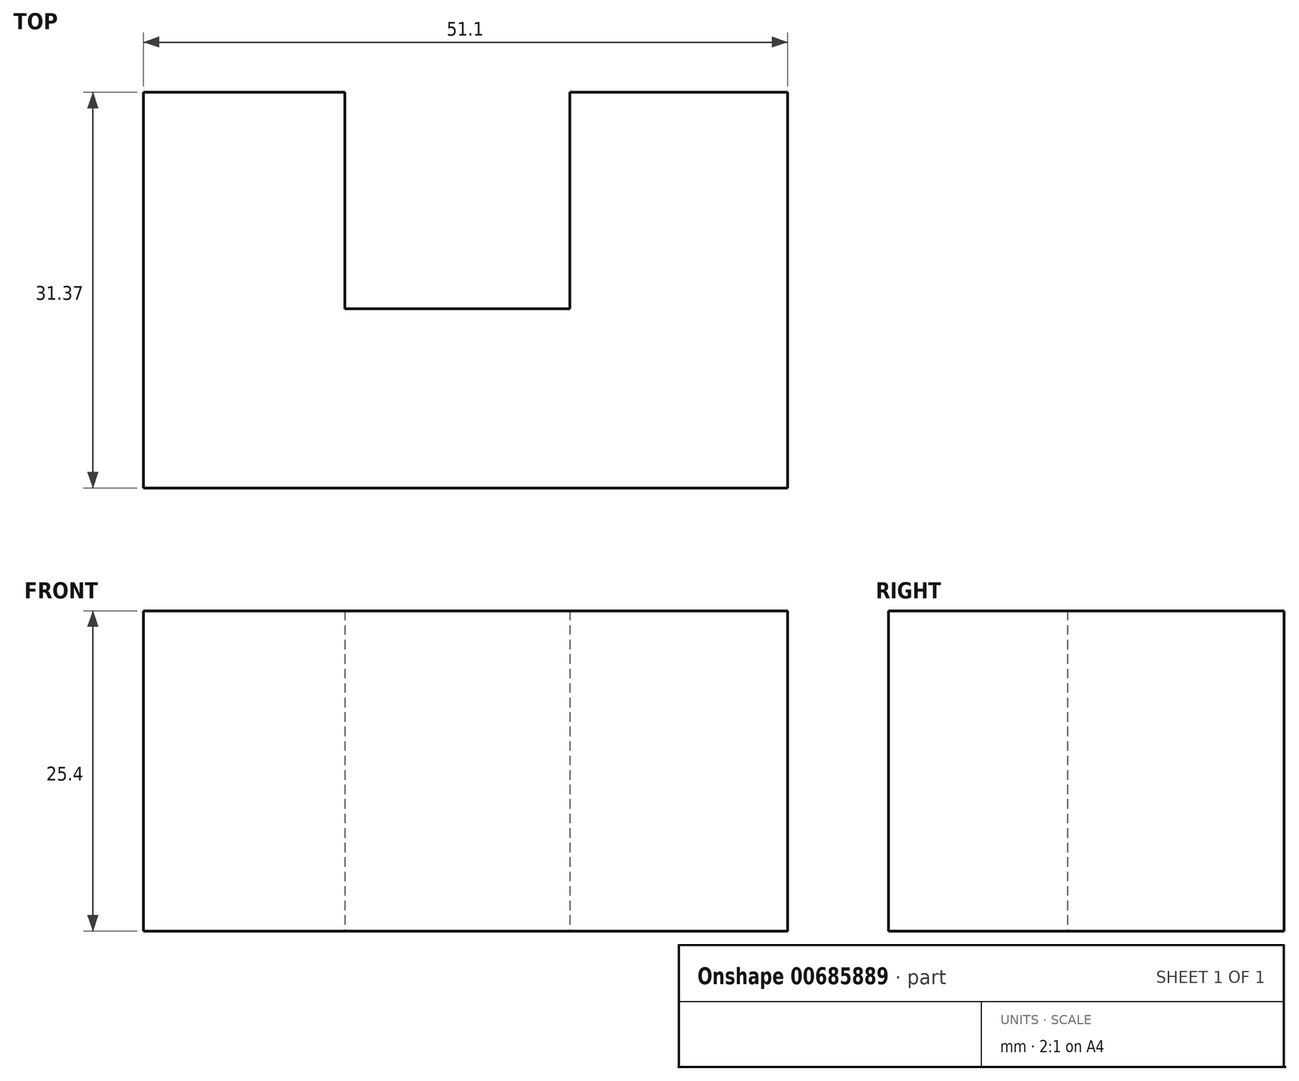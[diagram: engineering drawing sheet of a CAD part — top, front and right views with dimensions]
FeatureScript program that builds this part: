
annotation { "Feature Type Name" : "Feature", "Feature Type Description" : "" }
export const myFeature = defineFeature(function(context is Context, id is Id, definition is map)
    precondition{}
    {
        {
            var Q0;
            Q0=qCreatedBy(makeId("Top.planeOp"),FACE);
            var sketch = newSketch(context, id + "F0", { "sketchPlane" : qUnion([Q0])});
            skLineSegment(sketch, "E0", {"start": v(0, 0) * mm, "end": v(-8.98, 0) * mm});
            skLineSegment(sketch, "E1", {"start": v(-8.98, 0) * mm, "end": v(-33.84, 0) * mm});
            skLineSegment(sketch, "E2", {"start": v(-33.84, 0) * mm, "end": v(-33.84, 31.37) * mm});
            skLineSegment(sketch, "E3", {"start": v(-33.84, 31.37) * mm, "end": v(-17.86, 31.37) * mm});
            skLineSegment(sketch, "E4", {"start": v(-17.86, 31.37) * mm, "end": v(-17.86, 14.2) * mm});
            skLineSegment(sketch, "E5", {"start": v(-17.86, 14.2) * mm, "end": v(0, 14.2) * mm});
            skLineSegment(sketch, "E6", {"start": v(0, 14.2) * mm, "end": v(0, 31.37) * mm});
            skLineSegment(sketch, "E7", {"start": v(0, 31.37) * mm, "end": v(17.26, 31.37) * mm});
            skLineSegment(sketch, "E8", {"start": v(17.26, 31.37) * mm, "end": v(17.26, 0) * mm});
            skLineSegment(sketch, "E9", {"start": v(17.26, 0) * mm, "end": v(0, 0) * mm});
            skSolve(sketch);
        }
        {
            var Q0;
            Q0 = qSketchRegion(id + "F0", true);
            extrude(context, id + "F1", {"entities" : qUnion([Q0]), "depth" : 25.4 * mm, "offsetDistance" : 25.4 * mm});
        }
    });
